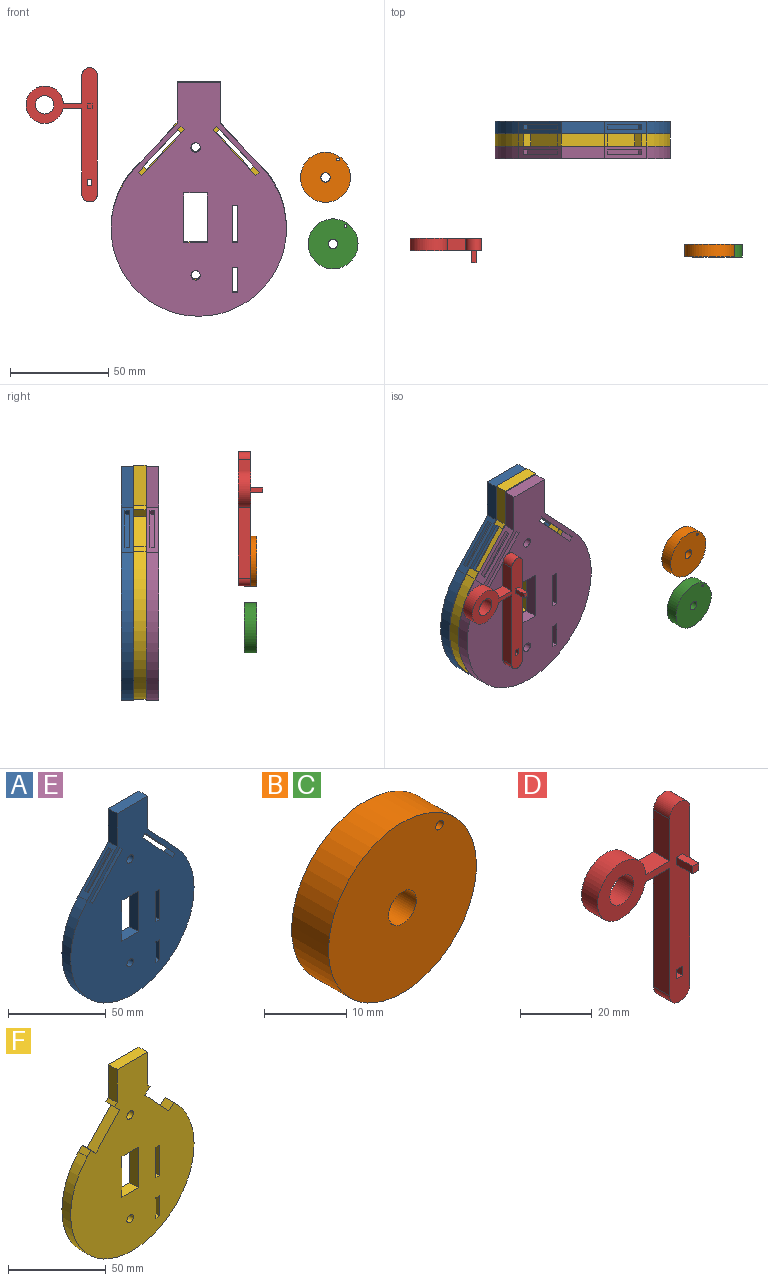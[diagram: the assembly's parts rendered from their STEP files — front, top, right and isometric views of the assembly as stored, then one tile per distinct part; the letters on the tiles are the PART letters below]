
ASSEMBLY  parts=6 mates=2
PART A: 38 faces, bbox 89.2x6.4x118.9 mm
  f0: plane 23.22x21.65mm, normal (0.73,0,0.68), area 137.1mm2, adj f4,f5,f28,f29,f34,f35,f36,f37
  f1: plane 23.22x21.65mm, normal (-0.73,0,-0.68), area 137.1mm2, adj f12,f13,f28,f29,f34,f35,f36,f37
  f2: plane 23.22x21.65mm, normal (-0.73,0,0.68), area 137.1mm2, adj f4,f27,f28,f29,f30,f31,f32,f33
  f3: plane 23.22x21.65mm, normal (0.73,0,-0.68), area 137.1mm2, adj f10,f21,f28,f29,f30,f31,f32,f33
  f4: cylinder r=44.61mm len=89.22mm, axis (0,1,0), area 1315mm2, adj f0,f2,f28,f29
  f5: plane 20.64x6.35mm, normal (1,0,0), area 131mm2, adj f0,f6,f28,f29
  f6: plane 21.95x6.35mm, normal (0,0,1), area 139.4mm2, adj f5,f27,f28,f29
  f7: plane 18.9x6.35mm, normal (1,0,0), area 120mm2, adj f8,f20,f28,f29
  f8: plane 6.35x2.79mm, normal (0,0,-1), area 17.7mm2, adj f7,f9,f28,f29
  f9: plane 18.9x6.35mm, normal (-1,0,0), area 120mm2, adj f8,f20,f28,f29
  f10: plane 6.35x1.86mm, normal (-0.68,0,-0.73), area 16.1mm2, adj f3,f11,f28,f29
  f11: plane 23.22x21.65mm, normal (-0.73,0,0.68), area 201.6mm2, adj f10,f21,f28,f29
  f12: plane 6.35x1.86mm, normal (0.68,0,-0.73), area 16.1mm2, adj f1,f22,f28,f29
  f13: plane 6.35x1.86mm, normal (-0.68,0,0.73), area 16.1mm2, adj f1,f22,f28,f29
  f14: plane 6.35x2.79mm, normal (0,0,-1), area 17.7mm2, adj f15,f25,f28,f29
  f15: plane 12.7x6.35mm, normal (-1,0,0), area 80.6mm2, adj f14,f16,f28,f29
  f16: plane 6.35x2.79mm, normal (0,0,1), area 17.7mm2, adj f15,f25,f28,f29
  f17: plane 11.96x6.35mm, normal (0,0,-1), area 76mm2, adj f18,f26,f28,f29
  f18: plane 25.4x6.35mm, normal (-1,0,0), area 161.3mm2, adj f17,f19,f28,f29
  f19: plane 11.96x6.35mm, normal (0,0,1), area 76mm2, adj f18,f26,f28,f29
  f20: plane 6.35x2.79mm, normal (0,0,1), area 17.7mm2, adj f7,f9,f28,f29
  f21: plane 6.35x1.86mm, normal (0.68,0,0.73), area 16.1mm2, adj f3,f11,f28,f29
  f22: plane 23.22x21.65mm, normal (0.73,0,0.68), area 201.6mm2, adj f12,f13,f28,f29
  f23: cylinder r=2.39mm len=6.35mm, axis (0,1,0), area 95.3mm2, adj f28,f29
  f24: cylinder r=2.39mm len=6.35mm, axis (0,1,0), area 95.3mm2, adj f28,f29
  f25: plane 12.7x6.35mm, normal (1,0,0), area 80.6mm2, adj f14,f16,f28,f29
  f26: plane 25.4x6.35mm, normal (1,0,0), area 161.3mm2, adj f17,f19,f28,f29
  f27: plane 20.64x6.35mm, normal (-1,0,0), area 131mm2, adj f2,f6,f28,f29
  f28: plane 118.89x89.22mm, normal (0,-1,0), area 6487.9mm2, adj f0,f1,f2,f3,f4,f5,f6,f7
  f29: plane 118.89x89.22mm, normal (0,1,0), area 6487.9mm2, adj f0,f1,f2,f3,f4,f5,f6,f7
  f30: plane 2.54x1.86mm, normal (-0.68,0,-0.73), area 6.5mm2, adj f2,f3,f31,f33
  f31: plane 20.31x19.18mm, normal (0,-1,0), area 64.5mm2, adj f2,f3,f30,f32
  f32: plane 2.54x1.86mm, normal (0.68,0,0.73), area 6.5mm2, adj f2,f3,f31,f33
  f33: plane 20.31x19.18mm, normal (0,1,0), area 64.5mm2, adj f2,f3,f30,f32
  f34: plane 2.54x1.86mm, normal (0.68,0,-0.73), area 6.5mm2, adj f0,f1,f35,f37
  f35: plane 20.31x19.18mm, normal (0,1,0), area 64.5mm2, adj f0,f1,f34,f36
  f36: plane 2.54x1.86mm, normal (-0.68,0,0.73), area 6.5mm2, adj f0,f1,f35,f37
  f37: plane 20.31x19.18mm, normal (0,-1,0), area 64.5mm2, adj f0,f1,f34,f36
PART B: 5 faces, bbox 25.4x6.4x25.4 mm
  f0: cylinder r=2.39mm len=6.35mm, axis (0,1,0), area 95.3mm2, adj f3,f4
  f1: cylinder r=0.65mm len=6.35mm, axis (0,1,0), area 25.9mm2, adj f3,f4
  f2: cylinder r=12.7mm len=25.4mm, axis (0,1,0), area 506.7mm2, adj f3,f4
  f3: plane 25.4x25.4mm, normal (0,-1,0), area 487.5mm2, adj f0,f1,f2
  f4: plane 25.4x25.4mm, normal (0,1,0), area 487.5mm2, adj f0,f1,f2
PART C: same geometry as B
PART D: 20 faces, bbox 36.3x12.6x68.3 mm
  f0: plane 6.35x3.18mm, normal (-1,0,0), area 20.2mm2, adj f1,f12,f13,f14
  f1: plane 6.35x2.41mm, normal (0,0,1), area 15.3mm2, adj f0,f2,f13,f14
  f2: plane 6.35x3.18mm, normal (1,0,0), area 20.2mm2, adj f1,f12,f13,f14
  f3: cylinder r=9.53mm len=19.05mm, axis (0,1,0), area 364.3mm2, adj f4,f10,f13,f14
  f4: plane 9.53x6.35mm, normal (0,0,-1), area 60.5mm2, adj f3,f5,f13,f14
  f5: plane 43.57x6.35mm, normal (-1,0,0), area 276.7mm2, adj f4,f6,f13,f14
  f6: cylinder r=3.97mm len=7.94mm, axis (0,1,0), area 79.2mm2, adj f5,f7,f13,f14
  f7: plane 60.33x6.35mm, normal (1,0,0), area 383.1mm2, adj f6,f8,f13,f14
  f8: cylinder r=3.97mm len=7.94mm, axis (0,1,0), area 79.2mm2, adj f7,f9,f13,f14
  f9: plane 14.29x6.35mm, normal (-1,0,0), area 90.7mm2, adj f8,f10,f13,f14
  f10: plane 9.35x6.35mm, normal (0,0,1), area 59.4mm2, adj f3,f9,f13,f14
  f11: cylinder r=4.7mm len=9.4mm, axis (0,1,0), area 187.6mm2, adj f13,f14
  f12: plane 6.35x2.41mm, normal (0,0,-1), area 15.3mm2, adj f0,f2,f13,f14
  f13: plane 68.26x36.32mm, normal (0,-1,0), area 753.2mm2, adj f0,f1,f2,f3,f4,f5,f6,f7
  f14: plane 68.26x36.32mm, normal (0,1,0), area 759.3mm2, adj f0,f1,f2,f3,f4,f5,f6,f7
  f15: plane 6.22x2.41mm, normal (0,0,-1), area 15mm2, adj f13,f16,f18,f19
  f16: plane 6.22x2.54mm, normal (-1,0,0), area 15.8mm2, adj f13,f15,f17,f19
  f17: plane 6.22x2.41mm, normal (0,0,1), area 15mm2, adj f13,f16,f18,f19
  f18: plane 6.22x2.54mm, normal (1,0,0), area 15.8mm2, adj f13,f15,f17,f19
  f19: plane 2.54x2.41mm, normal (0,-1,0), area 6.1mm2, adj f15,f16,f17,f18
PART E: same geometry as A
PART F: 30 faces, bbox 89.2x6.4x118.9 mm
  f0: plane 6.35x2.74mm, normal (0.73,0,0.68), area 23.8mm2, adj f1,f4,f23,f28
  f1: plane 118.89x89.22mm, normal (0,-1,0), area 6391.1mm2, adj f0,f2,f3,f4,f5,f6,f7,f8
  f2: plane 6.35x1.91mm, normal (-0.73,0,0.68), area 16.6mm2, adj f1,f22,f23,f24
  f3: plane 6.35x2.74mm, normal (-0.73,0,0.68), area 23.8mm2, adj f1,f4,f23,f25
  f4: cylinder r=44.61mm len=89.22mm, axis (0,1,0), area 1315mm2, adj f0,f1,f3,f23
  f5: plane 6.35x1.91mm, normal (0.73,0,0.68), area 16.6mm2, adj f1,f6,f23,f27
  f6: plane 20.64x6.35mm, normal (1,0,0), area 131mm2, adj f1,f5,f7,f23
  f7: plane 21.95x6.35mm, normal (0,0,1), area 139.4mm2, adj f1,f6,f22,f23
  f8: plane 18.9x6.35mm, normal (1,0,0), area 120mm2, adj f1,f9,f17,f23
  f9: plane 6.35x2.79mm, normal (0,0,-1), area 17.7mm2, adj f1,f8,f10,f23
  f10: plane 18.9x6.35mm, normal (-1,0,0), area 120mm2, adj f1,f9,f17,f23
  f11: plane 6.35x2.79mm, normal (0,0,-1), area 17.7mm2, adj f1,f12,f20,f23
  f12: plane 12.7x6.35mm, normal (-1,0,0), area 80.6mm2, adj f1,f11,f13,f23
  f13: plane 6.35x2.79mm, normal (0,0,1), area 17.7mm2, adj f1,f12,f20,f23
  f14: plane 11.96x6.35mm, normal (0,0,-1), area 76mm2, adj f1,f15,f21,f23
  f15: plane 25.4x6.35mm, normal (-1,0,0), area 161.3mm2, adj f1,f14,f16,f23
  f16: plane 11.96x6.35mm, normal (0,0,1), area 76mm2, adj f1,f15,f21,f23
  f17: plane 6.35x2.79mm, normal (0,0,1), area 17.7mm2, adj f1,f8,f10,f23
  f18: cylinder r=2.39mm len=6.35mm, axis (0,1,0), area 95.3mm2, adj f1,f23
  f19: cylinder r=2.39mm len=6.35mm, axis (0,1,0), area 95.3mm2, adj f1,f23
  f20: plane 12.7x6.35mm, normal (1,0,0), area 80.6mm2, adj f1,f11,f13,f23
  f21: plane 25.4x6.35mm, normal (1,0,0), area 161.3mm2, adj f1,f14,f16,f23
  f22: plane 20.64x6.35mm, normal (-1,0,0), area 131mm2, adj f1,f2,f7,f23
  f23: plane 118.89x89.22mm, normal (0,1,0), area 6391.1mm2, adj f0,f2,f3,f4,f5,f6,f7,f8
  f24: plane 6.35x3.72mm, normal (-0.68,0,-0.73), area 32.3mm2, adj f1,f2,f23,f26
  f25: plane 6.35x3.72mm, normal (0.68,0,0.73), area 32.3mm2, adj f1,f3,f23,f26
  f26: plane 18.58x17.32mm, normal (-0.73,0,0.68), area 161.3mm2, adj f1,f23,f24,f25
  f27: plane 6.35x3.72mm, normal (0.68,0,-0.73), area 32.3mm2, adj f1,f5,f23,f29
  f28: plane 6.35x3.72mm, normal (-0.68,0,0.73), area 32.3mm2, adj f0,f1,f23,f29
  f29: plane 18.58x17.32mm, normal (0.73,0,0.68), area 161.3mm2, adj f1,f23,f27,f28
PLACE A t=(-36.28,62.65,40.9)mm
PLACE B t=(29.76,0,36.48)mm
PLACE C t=(33.58,0,2.68)mm
PLACE D t=(-90.19,3.11,58.11)mm
PLACE E t=(-36.28,49.95,40.9)mm
PLACE F t=(-36.28,56.3,41.46)mm
MATE fastened E.f29 <-> F.f1  axis (0,1,0) through (-34.88,53.12,16.48)mm
MATE fastened F.f23 <-> A.f28  axis (0,1,0) through (-34.88,59.47,16.48)mm
